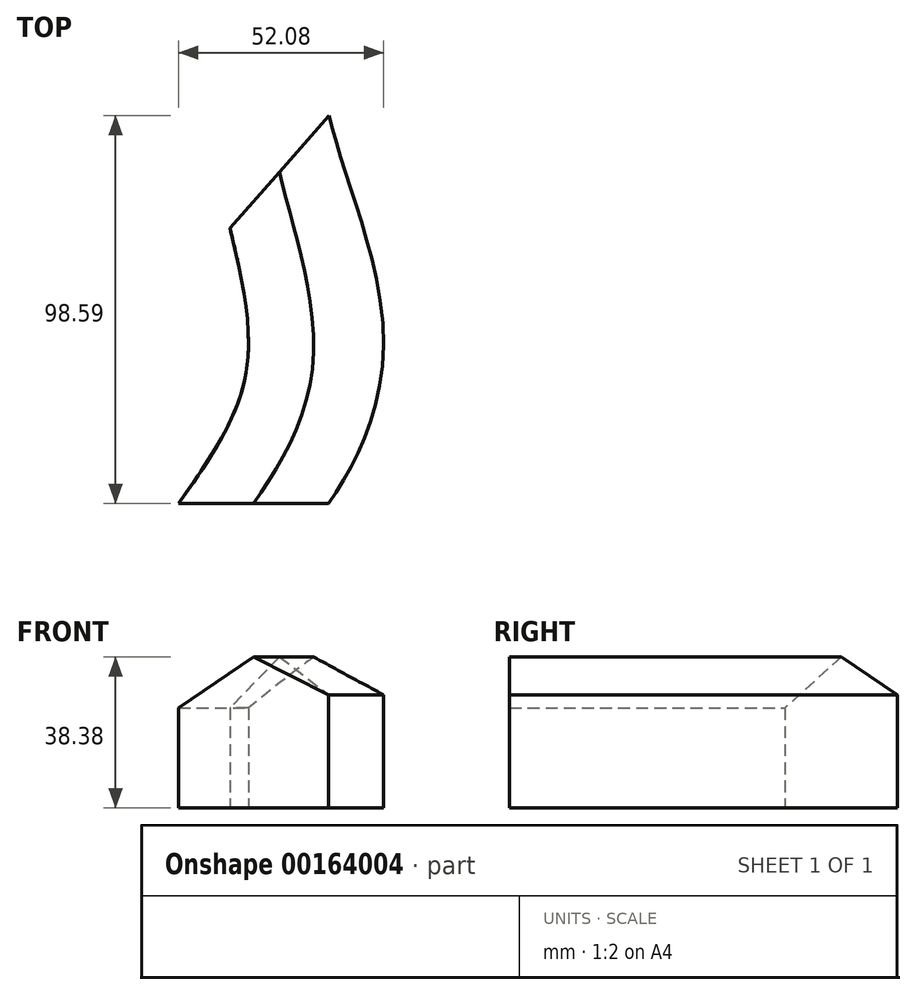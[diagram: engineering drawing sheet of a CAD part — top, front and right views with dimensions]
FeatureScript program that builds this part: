
annotation { "Feature Type Name" : "Feature", "Feature Type Description" : "" }
export const myFeature = defineFeature(function(context is Context, id is Id, definition is map)
    precondition{}
    {
        {
            var Q0;
            Q0=qCreatedBy(makeId("Front.planeOp"),FACE);
            var sketch = newSketch(context, id + "F0", { "sketchPlane" : qUnion([Q0])});
            skLineSegment(sketch, "E0", {"start": v(0, 0) * mm, "end": v(38.1, 0) * mm});
            skLineSegment(sketch, "E1", {"start": v(38.1, 51.35) * mm, "end": v(0, 25.4) * mm});
            skLineSegment(sketch, "E2", {"start": v(0, 25.4) * mm, "end": v(0, 0) * mm});
            skLineSegment(sketch, "E3", {"start": v(38.1, 0) * mm, "end": v(38.1, 51.35) * mm});
            skLineSegment(sketch, "E4", {"start": v(19.05, 38.38) * mm, "end": v(38.1, 28.77) * mm});
            skLineSegment(sketch, "E5", {"start": v(0, 0) * mm, "end": v(0, 103.56) * mm, "construction": true});
            skSolve(sketch);
        }
        {
            var Q0;
            Q0=qCreatedBy(makeId("Top.planeOp"),FACE);
            var sketch = newSketch(context, id + "F1", { "sketchPlane" : qUnion([Q0])});
            skFitSpline(sketch, "E6", {"points": [v(0, 0) * mm, v(17, 32.4) * mm, v(13.07, 69.93) * mm], "startDerivative": vector(44.68, 63.02) * mm, "endDerivative": vector(-18.37, 76.8) * mm});
            skSolve(sketch);
        }
        {
            var Q0;
            {var subQ1=sQuery(id+"F0.wireOp",EDGE,"E0");Q0=makeQuery(id+"F0.imprint","IMPRINT",FACE,{"disambiguationData":[TD([[makeQuery(id+"F0.imprint","IMPRINT",EDGE,{"derivedFrom":subQ1}),1.0]])]});}
            var Q1;
            Q1=sQuery(id+"F1.wireOp",EDGE,"E6");
            sweep(context, id + "F2", {"profiles" : qUnion([Q0]), "path" : qUnion([Q1])});
        }
    });
